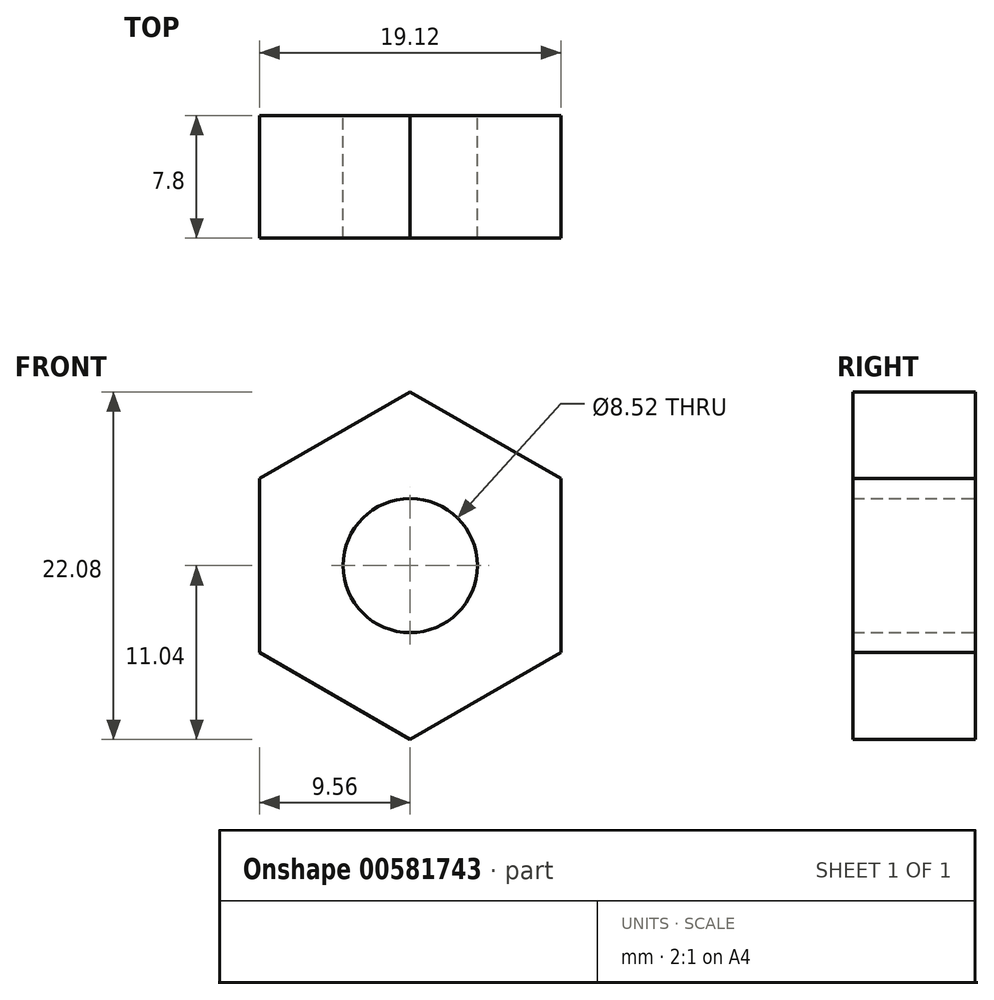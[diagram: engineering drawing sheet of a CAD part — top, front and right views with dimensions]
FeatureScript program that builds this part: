
annotation { "Feature Type Name" : "Feature", "Feature Type Description" : "" }
export const myFeature = defineFeature(function(context is Context, id is Id, definition is map)
    precondition{}
    {
        {
            var Q0;
            Q0=qCreatedBy(makeId("Front.planeOp"),FACE);
            var sketch = newSketch(context, id + "F0", { "sketchPlane" : qUnion([Q0])});
            skCircle(sketch, "E0.cCircle", {"center": v(0, 0) * mm, "radius": 9.56 * mm, "construction": true});
            skLineSegment(sketch, "E0.0", {"start": v(9.56, 5.52) * mm, "end": v(9.56, -5.52) * mm});
            skLineSegment(sketch, "E0.1", {"start": v(9.56, -5.52) * mm, "end": v(0, -11.04) * mm});
            skLineSegment(sketch, "E0.2", {"start": v(0, -11.04) * mm, "end": v(-9.56, -5.52) * mm});
            skLineSegment(sketch, "E0.3", {"start": v(-9.56, -5.52) * mm, "end": v(-9.56, 5.52) * mm});
            skLineSegment(sketch, "E0.4", {"start": v(-9.56, 5.52) * mm, "end": v(0, 11.04) * mm});
            skLineSegment(sketch, "E0.5", {"start": v(0, 11.04) * mm, "end": v(9.56, 5.52) * mm});
            skPoint(sketch, "E0.0.midPoint", {"position": v(9.56, 0) * mm});
            skCircle(sketch, "E1", {"center": v(0, 0) * mm, "radius": 4.26 * mm});
            skSolve(sketch);
        }
        {
            var Q0;
            Q0=makeQuery(id+"F0.imprint","IMPRINT",FACE,{"disambiguationData":[TD([[makeQuery(id+"F0.imprint","IMPRINT",EDGE,{"derivedFrom":sQuery(id+"F0.wireOp",EDGE,"E0.0")}),-1.0]])]});
            extrude(context, id + "F1", {"entities" : qUnion([Q0]), "depth" : 7.8 * mm, "offsetDistance" : 25 * mm});
        }
    });
